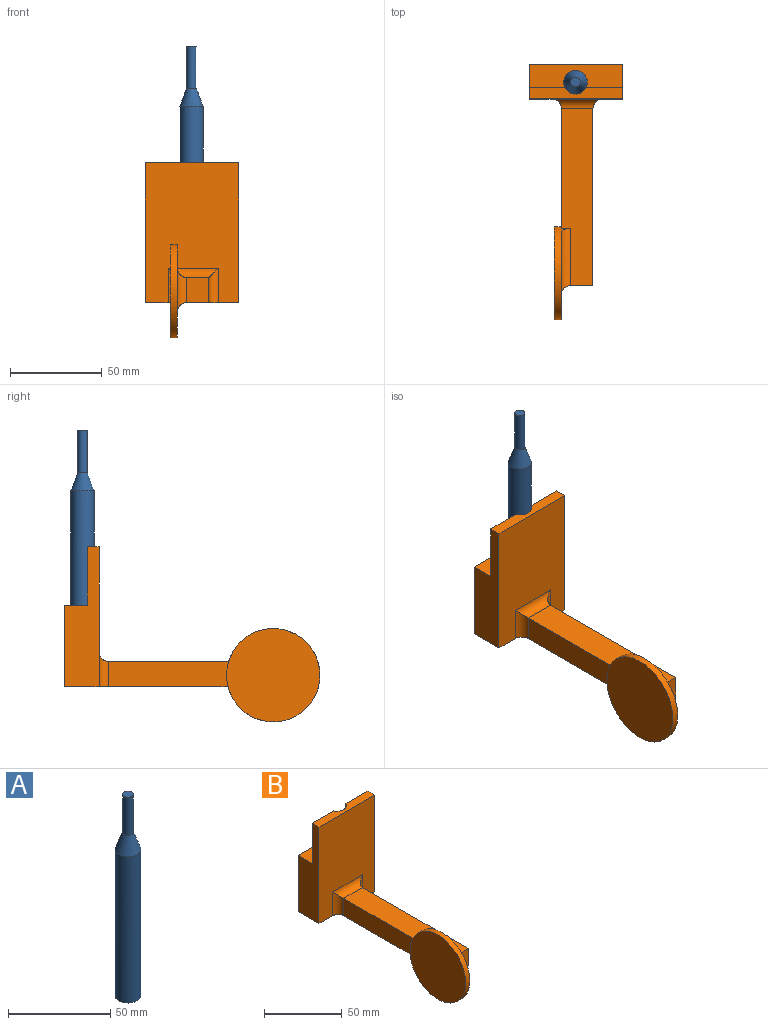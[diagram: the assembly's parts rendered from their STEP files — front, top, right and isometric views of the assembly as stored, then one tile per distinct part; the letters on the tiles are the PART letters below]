
ASSEMBLY  parts=2 mates=1
PART A: 5 faces, bbox 12.7x12.7x120.7 mm
  f0: cylinder r=6.35mm len=87.64mm, axis (0,0,-1), area 3496.8mm2, adj f1,f4
  f1: plane 12.7x12.7mm, normal (0,0,-1), area 126.7mm2, adj f0
  f2: cylinder r=2.67mm len=22.89mm, axis (0,0,-1), area 383.5mm2, adj f3,f4
  f3: plane 5.33x5.33mm, normal (0,0,1), area 22.3mm2, adj f2
  f4: cone r=1.27mm half-angle=20deg, axis (0,0,-1), area 305mm2, adj f0,f2
PART B: 24 faces, bbox 50.8x139.3x95.4 mm
  f0: plane 76.2x19.05mm, normal (-1,0,0), area 1048.4mm2, adj f3,f4,f5,f6,f7,f17
  f1: plane 76.2x19.05mm, normal (1,0,0), area 1048.4mm2, adj f2,f4,f5,f6,f7,f17
  f2: plane 31.75x19.82mm, normal (0,1,0), area 629.1mm2, adj f1,f5,f7,f8
  f3: plane 31.75x19.25mm, normal (0,1,0), area 611mm2, adj f0,f5,f7,f8
  f4: plane 76.2x50.8mm, normal (0,-1,0), area 3357.2mm2, adj f0,f1,f5,f6,f21,f22,f23
  f5: plane 50.8x6.35mm, normal (0,0,1), area 291.1mm2, adj f0,f1,f2,f3,f4,f8
  f6: plane 120.65x50.8mm, normal (0,0,-1), area 2565.3mm2, adj f0,f1,f4,f11,f12,f13,f15,f17
  f7: plane 50.8x12.7mm, normal (0,0,1), area 544.9mm2, adj f0,f1,f2,f3,f8,f17
  f8: cylinder r=6.48mm len=57.15mm, axis (0,0,1), area 1500.3mm2, adj f2,f3,f5,f7,f9
  f9: plane 12.95x12.95mm, normal (0,0,1), area 131.8mm2, adj f8
  f10: plane 96.52x17.18mm, normal (0,0,1), area 1500.9mm2, adj f11,f12,f13,f15,f20,f22
  f11: plane 65.47x13.71mm, normal (-1,0,0), area 886.5mm2, adj f6,f10,f15,f23
  f12: plane 96.52x13.71mm, normal (1,0,0), area 1323.2mm2, adj f6,f10,f13,f21
  f13: plane 13.71x12.1mm, normal (0,-1,0), area 165.9mm2, adj f6,f10,f12,f19
  f14: plane 50.8x48.13mm, normal (1,0,0), area 1161mm2, adj f15,f18,f19,f20
  f15: cylinder r=25.4mm len=50.8mm, axis (1,0,0), area 619.7mm2, adj f6,f10,f11,f14,f16,f18,f20
  f16: plane 50.8x50.8mm, normal (-1,0,0), area 2026.8mm2, adj f15
  f17: plane 50.8x44.45mm, normal (0,1,0), area 2258.1mm2, adj f0,f1,f6,f7
  f18: cylinder r=5.08mm len=36.47mm, axis (0,-1,0), area 260.4mm2, adj f6,f14,f15,f19
  f19: cylinder r=5.08mm len=23.87mm, axis (0,0,-1), area 138.9mm2, adj f13,f14,f18,f20
  f20: cylinder r=5.08mm len=36.13mm, axis (0,1,0), area 256.9mm2, adj f10,f14,f15,f19
  f21: cylinder r=5.08mm len=18.79mm, axis (0,0,-1), area 124.1mm2, adj f4,f6,f12,f22
  f22: cylinder r=5.08mm len=27.34mm, axis (1,0,0), area 166.6mm2, adj f4,f10,f21,f23
  f23: cylinder r=5.08mm len=18.79mm, axis (0,0,1), area 124.1mm2, adj f4,f6,f11,f22
PLACE A t=(25.11,-41.71,19.05)mm
PLACE B at identity fixed
MATE fastened A.f0 <-> B.f8  axis (0,0,-1) through (25.11,-41.71,19.05)mm
